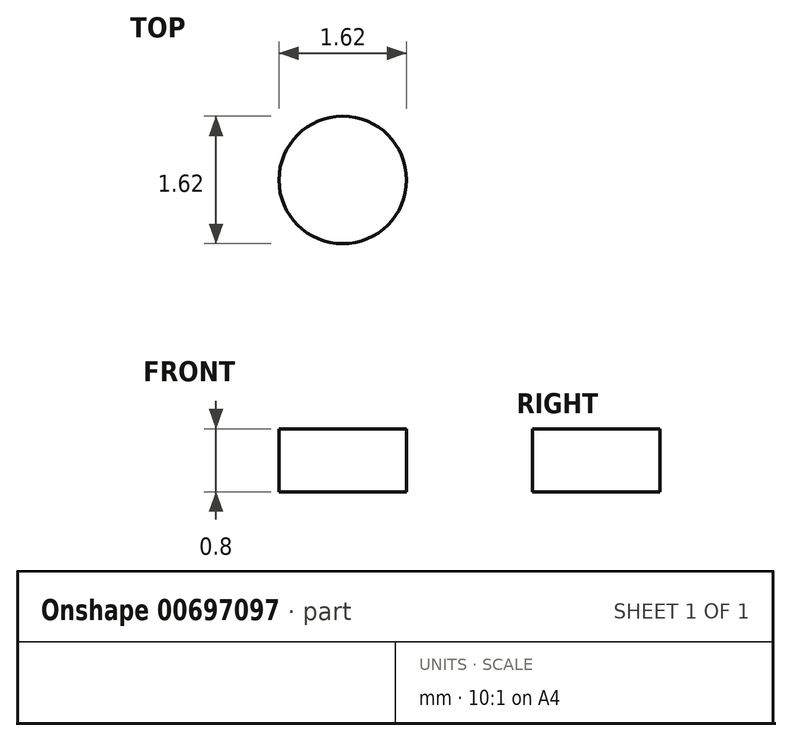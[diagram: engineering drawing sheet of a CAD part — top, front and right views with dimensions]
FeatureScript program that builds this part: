
annotation { "Feature Type Name" : "Feature", "Feature Type Description" : "" }
export const myFeature = defineFeature(function(context is Context, id is Id, definition is map)
    precondition{}
    {
        {
            var Q0;
            Q0=qCreatedBy(makeId("Top.planeOp"),FACE);
            var sketch = newSketch(context, id + "F0", { "sketchPlane" : qUnion([Q0])});
            skCircle(sketch, "E0", {"center": v(0, 0) * mm, "radius": 0.81 * mm});
            skSolve(sketch);
        }
        {
            var Q0;
            Q0 = qSketchRegion(id + "F0", true);
            extrude(context, id + "F1", {"entities" : qUnion([Q0]), "depth" : 0.8 * mm, "offsetDistance" : 25 * mm});
        }
    });
